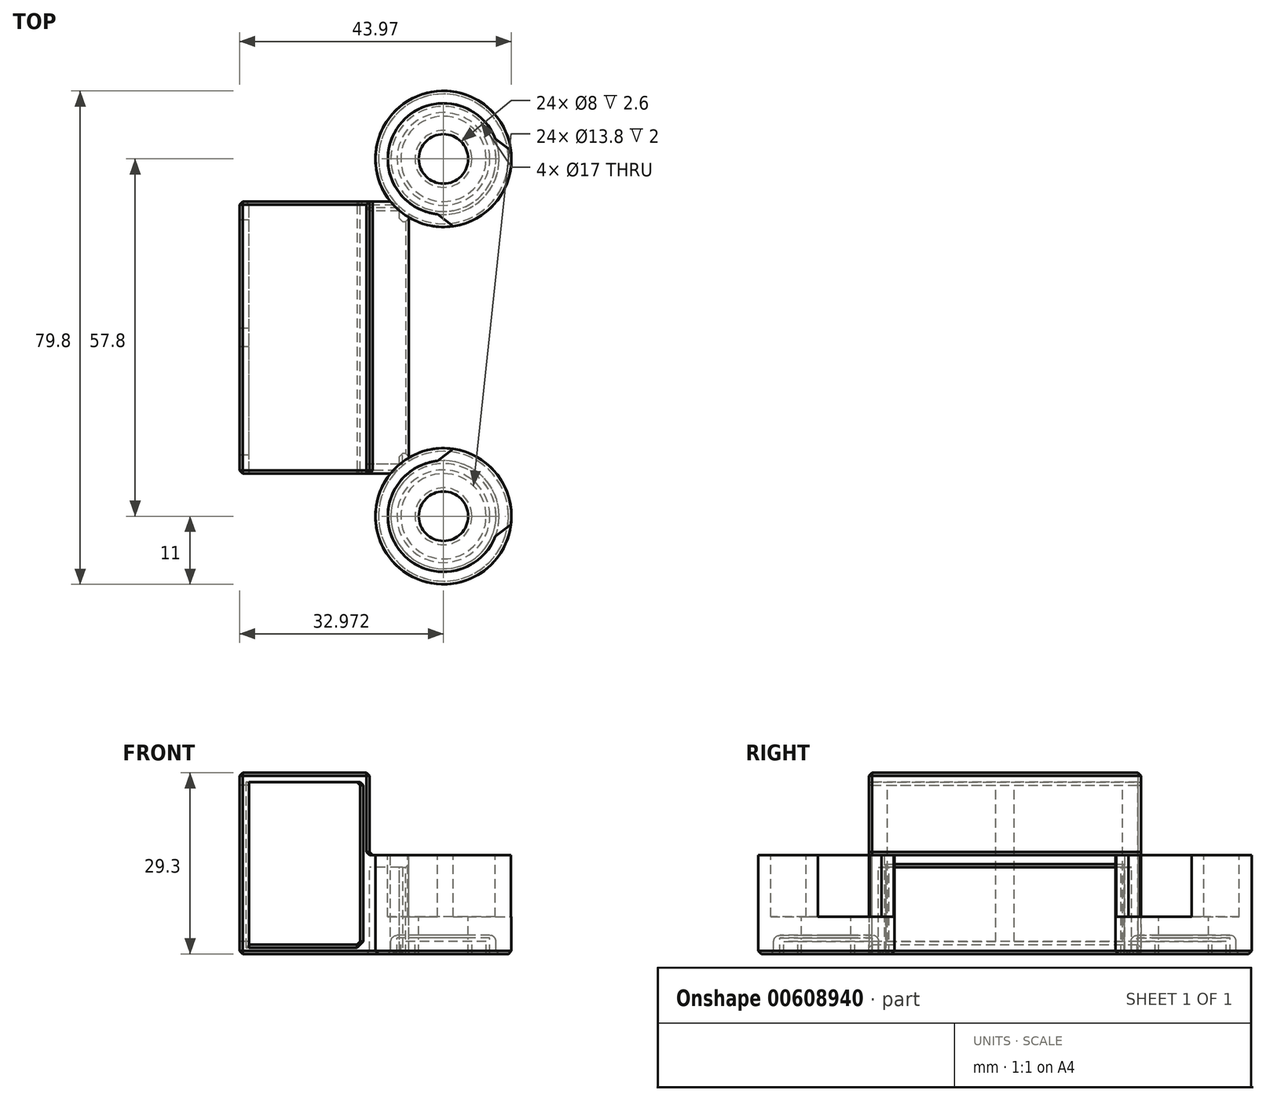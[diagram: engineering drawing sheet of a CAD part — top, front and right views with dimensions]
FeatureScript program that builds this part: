
annotation { "Feature Type Name" : "Feature", "Feature Type Description" : "" }
export const myFeature = defineFeature(function(context is Context, id is Id, definition is map)
    precondition{}
    {
        {
            var Q0;
            Q0=qCreatedBy(makeId("Front.planeOp"),FACE);
            var sketch = newSketch(context, id + "F0", { "sketchPlane" : qUnion([Q0])});
            skLineSegment(sketch, "E0.bottom", {"start": v(-19.5, 14.65) * mm, "end": v(1.5, 14.65) * mm});
            skLineSegment(sketch, "E0.top", {"start": v(-19.5, -14.65) * mm, "end": v(1.5, -14.65) * mm});
            skLineSegment(sketch, "E0.left", {"start": v(-19.5, 14.65) * mm, "end": v(-19.5, -14.65) * mm});
            skLineSegment(sketch, "E0.right", {"start": v(1.5, 14.65) * mm, "end": v(1.5, -14.65) * mm});
            skLineSegment(sketch, "E1.bottom", {"start": v(-18, 13.15) * mm, "end": v(0, 13.15) * mm});
            skLineSegment(sketch, "E1.top", {"start": v(-18, -13.15) * mm, "end": v(0, -13.15) * mm});
            skLineSegment(sketch, "E1.left", {"start": v(-18, 13.15) * mm, "end": v(-18, -13.15) * mm});
            skLineSegment(sketch, "E1.right", {"start": v(0, 13.15) * mm, "end": v(0, -13.15) * mm});
            skSolve(sketch);
        }
        {
            var Q0;
            Q0=makeQuery(id+"F0.imprint","IMPRINT",FACE,{"disambiguationData":[TD([[makeQuery(id+"F0.imprint","IMPRINT",EDGE,{"derivedFrom":sQuery(id+"F0.wireOp",EDGE,"E0.bottom")}),-1.0]])]});
            extrude(context, id + "F1", {"entities" : qUnion([Q0]), "depth" : 44 * mm, "offsetDistance" : 25 * mm});
        }
        {
            var Q0;
            Q0=makeQuery(id+"F1.opExtrude","SWEPT_FACE",FACE,{"disambiguationData":[OSD([sQuery(id+"F0.wireOp",EDGE,"E0.top")])]});
            cPlane(context, id + "F2", {"entities" : qUnion([Q0]), "cplaneType" : CPlaneType.OFFSET, "offset" : 16 * mm, "oppositeDirection" : true, "width" : 150 * mm, "height" : 150 * mm});
        }
        {
            var Q0;
            Q0=qCreatedBy(id+"F2.planeOp",FACE);
            var sketch = newSketch(context, id + "F3", { "sketchPlane" : qUnion([Q0])});
            skPoint(sketch, "E2.middle.positionSnap0", {"position": v(1.5, 22) * mm});
            skPoint(sketch, "E2.centerSnap0", {"position": v(1.5, 22) * mm});
            skLineSegment(sketch, "E3.bottom", {"start": v(1.5, 0) * mm, "end": v(7.87, 0) * mm});
            skLineSegment(sketch, "E3.top", {"start": v(1.5, 44) * mm, "end": v(7.87, 44) * mm});
            skLineSegment(sketch, "E3.left", {"start": v(1.5, 0) * mm, "end": v(1.5, 44) * mm});
            skLineSegment(sketch, "E3.right", {"start": v(7.87, 0) * mm, "end": v(7.87, 44) * mm});
            skPoint(sketch, "E3.middle", {"position": v(4.69, 22) * mm});
            skLineSegment(sketch, "E4.0", {"start": v(1.5, 42.5) * mm, "end": v(6.37, 42.5) * mm});
            skLineSegment(sketch, "E4.1", {"start": v(6.37, 1.5) * mm, "end": v(6.37, 42.5) * mm});
            skLineSegment(sketch, "E4.2", {"start": v(1.5, 1.5) * mm, "end": v(6.37, 1.5) * mm});
            skLineSegment(sketch, "E5", {"start": v(1.5, 1.5) * mm, "end": v(1.5, 42.5) * mm});
            skLineSegment(sketch, "E6", {"start": v(7.87, 3.25) * mm, "end": v(6.37, 3.25) * mm});
            skLineSegment(sketch, "E7", {"start": v(6.37, 40.75) * mm, "end": v(7.87, 40.75) * mm});
            skSolve(sketch);
        }
        {
            var Q0;
            {var subQ4=sQuery(id+"F3.wireOp",EDGE,"E3.bottom");Q0=makeQuery(id+"F3.imprint","IMPRINT",FACE,{"disambiguationData":[TD([[makeQuery(id+"F3.imprint","IMPRINT",EDGE,{"derivedFrom":subQ4}),1.0]])]});}
            var Q1;
            {var subQ0=sQuery(id+"F3.wireOp",EDGE,"E6");Q1=makeQuery(id+"F3.imprint","IMPRINT",FACE,{"disambiguationData":[TD([[makeQuery(id+"F3.imprint","IMPRINT",EDGE,{"derivedFrom":subQ0}),-1.0]])]});}
            var Q2;
            {var subQ1=sQuery(id+"F3.wireOp",EDGE,"E4.0");Q2=makeQuery(id+"F3.imprint","IMPRINT",FACE,{"disambiguationData":[TD([[makeQuery(id+"F3.imprint","IMPRINT",EDGE,{"derivedFrom":subQ1}),-1.0]])]});}
            var Q3;
            {var subQ2=sQuery(id+"F3.wireOp",EDGE,"E3.top");Q3=makeQuery(id+"F3.imprint","IMPRINT",FACE,{"disambiguationData":[TD([[makeQuery(id+"F3.imprint","IMPRINT",EDGE,{"derivedFrom":subQ2}),-1.0]])]});}
            extrude(context, id + "F4", {"entities" : qUnion([Q0, Q1, Q2, Q3]), "operationType" : NewBodyOperationType.ADD, "depth" : 2 * mm, "offsetDistance" : 25 * mm});
        }
        {
            var Q0;
            {var subQ4=sQuery(id+"F3.wireOp",EDGE,"E3.bottom");Q0=makeQuery(id+"F3.imprint","IMPRINT",FACE,{"disambiguationData":[TD([[makeQuery(id+"F3.imprint","IMPRINT",EDGE,{"derivedFrom":subQ4}),1.0]])]});}
            var Q1;
            {var subQ2=sQuery(id+"F3.wireOp",EDGE,"E3.top");Q1=makeQuery(id+"F3.imprint","IMPRINT",FACE,{"disambiguationData":[TD([[makeQuery(id+"F3.imprint","IMPRINT",EDGE,{"derivedFrom":subQ2}),-1.0]])]});}
            var Q2;
            Q2=makeQuery(id+"F1.opExtrude","SWEPT_FACE",FACE,{"disambiguationData":[OSD([sQuery(id+"F0.wireOp",EDGE,"E0.top")])]});
            extrude(context, id + "F5", {"entities" : qUnion([Q0, Q1]), "operationType" : NewBodyOperationType.ADD, "endBound" : BoundingType.UP_TO_SURFACE, "depth" : 20 * mm, "endBoundEntityFace" : qUnion([Q2]), "offsetDistance" : 25 * mm});
        }
        {
            var Q0;
            {var subQ0=sQuery(id+"F3.wireOp",EDGE,"E4.1");var subQ1=sQuery(id+"F3.wireOp",EDGE,"E3.right");var subQ2=sQuery(id+"F3.wireOp",EDGE,"E3.left");Q0=makeQuery(id+"F5.boolean.opBoolean","MERGE",FACE,{"derivedFrom":[makeQuery(id+"F1.opExtrude","SWEPT_FACE",FACE,{"disambiguationData":[OSD([sQuery(id+"F0.wireOp",EDGE,"E0.top")])]}),makeQuery(id+"F5.opExtrude","CAP_FACE",FACE,{"disambiguationData":[OSD([sQuery(id+"F3.wireOp",EDGE,"E3.bottom"),subQ2,subQ1,subQ0,sQuery(id+"F3.wireOp",EDGE,"E4.2"),sQuery(id+"F3.wireOp",EDGE,"E6")])],"isStart":false}),makeQuery(id+"F5.opExtrude","CAP_FACE",FACE,{"disambiguationData":[OSD([sQuery(id+"F3.wireOp",EDGE,"E3.top"),subQ2,subQ1,sQuery(id+"F3.wireOp",EDGE,"E4.0"),subQ0,sQuery(id+"F3.wireOp",EDGE,"E7")])],"isStart":false})]});}
            var sketch = newSketch(context, id + "F6", { "sketchPlane" : qUnion([Q0])});
            skLineSegment(sketch, "E8", {"start": v(-24.95, 22) * mm, "end": v(15.2, 22) * mm, "construction": true});
            skPoint(sketch, "E8.startSnap0", {"position": v(-19.5, 22) * mm});
            skLineSegment(sketch, "E9.0", {"start": v(-18, 0) * mm, "end": v(0, 0) * mm});
            skLineSegment(sketch, "E10.0", {"start": v(-18, 0) * mm, "end": v(0, 0) * mm, "construction": true});
            skLineSegment(sketch, "E11", {"start": v(-9, -14.84) * mm, "end": v(-9, 47.2) * mm, "construction": true});
            skPoint(sketch, "E11.startSnap0", {"position": v(-9, 0) * mm});
            skLineSegment(sketch, "E12", {"start": v(-9, 22) * mm, "end": v(20.33, -16.25) * mm, "construction": true});
            skLineSegment(sketch, "E13", {"start": v(-9, -8) * mm, "end": v(23.93, -8) * mm, "construction": true});
            skPoint(sketch, "E14", {"position": v(14, -8) * mm});
            skSolve(sketch);
        }
        {
            var Q0;
            {var subQ0=sQuery(id+"F3.wireOp",EDGE,"E3.right");Q0=makeQuery(id+"F5.boolean.opBoolean","MERGE",FACE,{"derivedFrom":[makeQuery(id+"F4.opExtrude","SWEPT_FACE",FACE,{"disambiguationData":[OSD([subQ0])]}),makeQuery(id+"F5.opExtrude","SWEPT_FACE",FACE,{"disambiguationData":[OSD([subQ0]),TDD([makeQuery(id+"F3.imprint","IMPRINT",EDGE,{"disambiguationData":[TD([[makeQuery(id+"F3.imprint","INTERSECT",VERTEX,{"derivedFrom":[sQuery(id+"F3.wireOp",EDGE,"E3.bottom"),subQ0]}),-1.0]])],"derivedFrom":subQ0})])]}),makeQuery(id+"F5.opExtrude","SWEPT_FACE",FACE,{"disambiguationData":[OSD([subQ0]),TDD([makeQuery(id+"F3.imprint","IMPRINT",EDGE,{"disambiguationData":[TD([[makeQuery(id+"F3.imprint","INTERSECT",VERTEX,{"derivedFrom":[sQuery(id+"F3.wireOp",EDGE,"E3.top"),subQ0]}),1.0]])],"derivedFrom":subQ0})])]})]});}
            cPlane(context, id + "F7", {"entities" : qUnion([Q0]), "cplaneType" : CPlaneType.OFFSET, "offset" : 5.6 * mm, "width" : 150 * mm, "height" : 150 * mm});
        }
        {
            var Q0;
            Q0=qCreatedBy(id+"F7.planeOp",FACE);
            var sketch = newSketch(context, id + "F8", { "sketchPlane" : qUnion([Q0])});
            skLineSegment(sketch, "E15", {"start": v(6.9, -11.65) * mm, "end": v(15.4, -11.65) * mm});
            skLineSegment(sketch, "E16", {"start": v(15.4, -11.65) * mm, "end": v(15.4, -14.65) * mm});
            skLineSegment(sketch, "E17", {"start": v(15.4, -14.65) * mm, "end": v(17.9, -14.65) * mm});
            skLineSegment(sketch, "E18", {"start": v(17.9, -14.65) * mm, "end": v(17.9, 1.35) * mm});
            skLineSegment(sketch, "E19", {"start": v(17.9, 1.35) * mm, "end": v(15.9, 1.35) * mm});
            skLineSegment(sketch, "E20", {"start": v(15.9, 1.35) * mm, "end": v(15.9, -8.65) * mm});
            skLineSegment(sketch, "E21", {"start": v(15.9, -8.65) * mm, "end": v(6.9, -8.65) * mm});
            skLineSegment(sketch, "E22", {"start": v(6.9, -8.65) * mm, "end": v(6.9, -11.65) * mm, "construction": true});
            skLineSegment(sketch, "E23", {"start": v(10.9, -8.65) * mm, "end": v(10.9, -11.65) * mm});
            skLineSegment(sketch, "E24", {"start": v(10.9, -14.65) * mm, "end": v(10.9, -12.05) * mm});
            skLineSegment(sketch, "E25", {"start": v(10.9, -14.65) * mm, "end": v(11.5, -14.65) * mm});
            skLineSegment(sketch, "E26", {"start": v(11.5, -14.65) * mm, "end": v(11.5, -12.65) * mm});
            skLineSegment(sketch, "E27", {"start": v(11.5, -12.05) * mm, "end": v(10.9, -12.05) * mm});
            skPoint(sketch, "E28.visualSharp", {"position": v(17.9, -14.65) * mm});
            skLineSegment(sketch, "E29", {"start": v(17.9, -14.15) * mm, "end": v(17.4, -14.65) * mm});
            skLineSegment(sketch, "E30", {"start": v(15.4, -14.15) * mm, "end": v(15.9, -14.65) * mm});
            skLineSegment(sketch, "E31", {"start": v(11.5, -12.05) * mm, "end": v(14.4, -12.05) * mm});
            skLineSegment(sketch, "E32", {"start": v(14.4, -12.05) * mm, "end": v(14.4, -14.65) * mm});
            skLineSegment(sketch, "E33", {"start": v(14.4, -14.65) * mm, "end": v(13.8, -14.65) * mm});
            skLineSegment(sketch, "E34", {"start": v(13.8, -14.65) * mm, "end": v(13.8, -12.65) * mm});
            skLineSegment(sketch, "E35", {"start": v(13.8, -12.65) * mm, "end": v(11.5, -12.65) * mm});
            skSolve(sketch);
        }
        {
            var Q0;
            Q0=makeQuery(id+"F8.imprint","IMPRINT",FACE,{"disambiguationData":[TD([[makeQuery(id+"F8.imprint","IMPRINT",EDGE,{"derivedFrom":sQuery(id+"F8.wireOp",EDGE,"E15")}),1.0]])]});
            var Q1;
            Q1=makeQuery(id+"F8.imprint","IMPRINT",FACE,{"disambiguationData":[TD([[makeQuery(id+"F8.imprint","IMPRINT",EDGE,{"derivedFrom":sQuery(id+"F8.wireOp",EDGE,"E24")}),-1.0]])]});
            var Q2;
            Q2=sQuery(id+"F8.wireOp",EDGE,"E22");
            revolve(context, id + "F9", {"entities" : qUnion([Q0, Q1]), "axis" : qUnion([Q2]), "revolveType" : RevolveType.FULL});
        }
        {
            var Q0;
            Q0=makeQuery(id+"F9.opRevolve","SWEPT_EDGE",EDGE,{"disambiguationData":[OSD([sQuery(id+"F8.wireOp",EDGE,"E15"),sQuery(id+"F8.wireOp",EDGE,"E16")])]});
            fillet(context, id + "F10", {"entities" : qUnion([Q0]), "radius" : 1 * mm, "tangentPropagation" : true, "allowEdgeOverflow" : false});
        }
        {
            var Q0;
            Q0=makeQuery(id+"F9.opRevolve","SWEPT_FACE",FACE,{"disambiguationData":[OSD([sQuery(id+"F8.wireOp",EDGE,"E19")])]});
            var sketch = newSketch(context, id + "F11", { "sketchPlane" : qUnion([Q0])});
            skLineSegment(sketch, "E36.0", {"start": v(-9, -22) * mm, "end": v(20.33, 16.25) * mm});
            skPoint(sketch, "E37.0", {"position": v(13.47, 6.9) * mm});
            skLineSegment(sketch, "E38.0", {"start": v(-9, -22) * mm, "end": v(20.33, 16.25) * mm, "construction": true});
            skLineSegment(sketch, "E39.right", {"start": v(8.79, 0.79) * mm, "end": v(18.16, 13.01) * mm});
            skLineSegment(sketch, "E40", {"start": v(18.16, 13.01) * mm, "end": v(26.99, 6.24) * mm});
            skLineSegment(sketch, "E41", {"start": v(26.99, 6.24) * mm, "end": v(17.61, -5.98) * mm});
            skLineSegment(sketch, "E42", {"start": v(17.61, -5.98) * mm, "end": v(8.79, 0.79) * mm});
            skLineSegment(sketch, "E43", {"start": v(22.3, 0.13) * mm, "end": v(13.47, 6.9) * mm, "construction": true});
            skLineSegment(sketch, "E44", {"start": v(13.47, 6.9) * mm, "end": v(4.35, 13.9) * mm, "construction": true});
            skSolve(sketch);
        }
        {
            var Q0;
            {var subQ0=sQuery(id+"F11.wireOp",EDGE,"E40");var subQ1=sQuery(id+"F8.wireOp",EDGE,"E19");var subQ2=makeQuery(id+"F9.opRevolve","SWEPT_EDGE",EDGE,{"disambiguationData":[OSD([sQuery(id+"F8.wireOp",EDGE,"E18"),subQ1])]});var subQ3=makeQuery(id+"F11.imprint","INTERSECT",VERTEX,{"derivedFrom":[subQ2,subQ0]});Q0=makeQuery(id+"F11.imprint","IMPRINT",FACE,{"disambiguationData":[TD([[makeQuery(id+"F11.imprint","IMPRINT",EDGE,{"disambiguationData":[TD([[subQ3,1.0]])],"derivedFrom":subQ0}),-1.0]])]});}
            extrude(context, id + "F12", {"entities" : qUnion([Q0]), "operationType" : NewBodyOperationType.REMOVE, "oppositeDirection" : true, "depth" : 10 * mm, "offsetDistance" : 25 * mm});
        }
        {
            var Q0;
            Q0=sQuery(id+"F6.wireOp",EDGE,"E8");
            cPlane(context, id + "F13", {"entities" : qUnion([Q0]), "cplaneType" : CPlaneType.LINE_ANGLE, "offset" : 12.5 * mm, "angle" : 0 * degree, "width" : 150 * mm, "height" : 150 * mm});
        }
        {
            var Q0;
            Q0=makeQuery(id+"F9.opRevolve","SWEPT_BODY",BODY,{"disambiguationData":[OSD([sQuery(id+"F8.wireOp",EDGE,"E15"),sQuery(id+"F8.wireOp",EDGE,"E16"),sQuery(id+"F8.wireOp",EDGE,"E17"),sQuery(id+"F8.wireOp",EDGE,"E18"),sQuery(id+"F8.wireOp",EDGE,"E19"),sQuery(id+"F8.wireOp",EDGE,"E20"),sQuery(id+"F8.wireOp",EDGE,"E21"),sQuery(id+"F8.wireOp",EDGE,"E23"),sQuery(id+"F8.wireOp",EDGE,"E29"),sQuery(id+"F8.wireOp",EDGE,"E30")])]});
            var Q1;
            Q1=makeQuery(id+"F9.opRevolve","SWEPT_BODY",BODY,{"disambiguationData":[OSD([sQuery(id+"F8.wireOp",EDGE,"E24"),sQuery(id+"F8.wireOp",EDGE,"E25"),sQuery(id+"F8.wireOp",EDGE,"E26"),sQuery(id+"F8.wireOp",EDGE,"E27")])]});
            var Q2;
            Q2=qCreatedBy(id+"F13.planeOp",FACE);
            mirror(context, id + "F14", {"entities" : qUnion([Q0, Q1]), "mirrorPlane" : qUnion([Q2])});
        }
        {
            var Q0;
            Q0=makeQuery(id+"F14.opPattern","COPY",BODY,{"derivedFrom":makeQuery(id+"F9.opRevolve","SWEPT_BODY",BODY,{"disambiguationData":[OSD([sQuery(id+"F8.wireOp",EDGE,"E15"),sQuery(id+"F8.wireOp",EDGE,"E16"),sQuery(id+"F8.wireOp",EDGE,"E17"),sQuery(id+"F8.wireOp",EDGE,"E18"),sQuery(id+"F8.wireOp",EDGE,"E19"),sQuery(id+"F8.wireOp",EDGE,"E20"),sQuery(id+"F8.wireOp",EDGE,"E21"),sQuery(id+"F8.wireOp",EDGE,"E23"),sQuery(id+"F8.wireOp",EDGE,"E29"),sQuery(id+"F8.wireOp",EDGE,"E30")])]}),"instanceName":"1"});
            var Q1;
            Q1=makeQuery(id+"F9.opRevolve","SWEPT_BODY",BODY,{"disambiguationData":[OSD([sQuery(id+"F8.wireOp",EDGE,"E15"),sQuery(id+"F8.wireOp",EDGE,"E16"),sQuery(id+"F8.wireOp",EDGE,"E17"),sQuery(id+"F8.wireOp",EDGE,"E18"),sQuery(id+"F8.wireOp",EDGE,"E19"),sQuery(id+"F8.wireOp",EDGE,"E20"),sQuery(id+"F8.wireOp",EDGE,"E21"),sQuery(id+"F8.wireOp",EDGE,"E23"),sQuery(id+"F8.wireOp",EDGE,"E29"),sQuery(id+"F8.wireOp",EDGE,"E30")])]});
            var Q2;
            Q2=makeQuery(id+"F1.opExtrude","SWEPT_BODY",BODY,{"disambiguationData":[OSD([sQuery(id+"F0.wireOp",EDGE,"E0.bottom"),sQuery(id+"F0.wireOp",EDGE,"E0.top"),sQuery(id+"F0.wireOp",EDGE,"E0.left"),sQuery(id+"F0.wireOp",EDGE,"E0.right"),sQuery(id+"F0.wireOp",EDGE,"E1.bottom"),sQuery(id+"F0.wireOp",EDGE,"E1.top"),sQuery(id+"F0.wireOp",EDGE,"E1.left"),sQuery(id+"F0.wireOp",EDGE,"E1.right")])]});
            booleanBodies(context, id + "F15", {"operationType" : BooleanOperationType.UNION, "tools" : qUnion([Q0, Q1, Q2])});
        }
        {
            var Q0;
            Q0=makeQuery(id+"F1.opExtrude","SWEPT_FACE",FACE,{"disambiguationData":[OSD([sQuery(id+"F0.wireOp",EDGE,"E0.left")])]});
            var sketch = newSketch(context, id + "F16", { "sketchPlane" : qUnion([Q0])});
            skLineSegment(sketch, "E45.bottom", {"start": v(41, -12.65) * mm, "end": v(23.5, -12.65) * mm});
            skLineSegment(sketch, "E45.top", {"start": v(41, 12.65) * mm, "end": v(23.5, 12.65) * mm});
            skLineSegment(sketch, "E45.left", {"start": v(41, -12.65) * mm, "end": v(41, 12.65) * mm});
            skLineSegment(sketch, "E45.right", {"start": v(23.5, -12.65) * mm, "end": v(23.5, 12.65) * mm});
            skLineSegment(sketch, "E46.bottom", {"start": v(20.5, -12.65) * mm, "end": v(3, -12.65) * mm});
            skLineSegment(sketch, "E46.top", {"start": v(20.5, 12.65) * mm, "end": v(3, 12.65) * mm});
            skLineSegment(sketch, "E46.left", {"start": v(20.5, -12.65) * mm, "end": v(20.5, 12.65) * mm});
            skLineSegment(sketch, "E46.right", {"start": v(3, -12.65) * mm, "end": v(3, 12.65) * mm});
            skSolve(sketch);
        }
        {
            var Q0;
            Q0=makeQuery(id+"F16.imprint","IMPRINT",FACE,{"disambiguationData":[TD([[makeQuery(id+"F16.imprint","IMPRINT",EDGE,{"derivedFrom":sQuery(id+"F16.wireOp",EDGE,"E46.bottom")}),-1.0]])]});
            var Q1;
            Q1=makeQuery(id+"F16.imprint","IMPRINT",FACE,{"disambiguationData":[TD([[makeQuery(id+"F16.imprint","IMPRINT",EDGE,{"derivedFrom":sQuery(id+"F16.wireOp",EDGE,"E45.bottom")}),-1.0]])]});
            var Q2;
            Q2=makeQuery(id+"F1.opExtrude","SWEPT_FACE",FACE,{"disambiguationData":[OSD([sQuery(id+"F0.wireOp",EDGE,"E1.left")])]});
            extrude(context, id + "F17", {"entities" : qUnion([Q0, Q1]), "operationType" : NewBodyOperationType.REMOVE, "endBound" : BoundingType.UP_TO_SURFACE, "oppositeDirection" : true, "depth" : 25 * mm, "endBoundEntityFace" : qUnion([Q2]), "offsetDistance" : 25 * mm});
        }
        {
            var Q0;
            Q0=makeQuery(id+"F1.opExtrude","SWEPT_EDGE",EDGE,{"disambiguationData":[OSD([sQuery(id+"F0.wireOp",EDGE,"E0.bottom"),sQuery(id+"F0.wireOp",EDGE,"E0.left")])]});
            var Q1;
            Q1=makeQuery(id+"F1.opExtrude","SWEPT_EDGE",EDGE,{"disambiguationData":[OSD([sQuery(id+"F0.wireOp",EDGE,"E0.top"),sQuery(id+"F0.wireOp",EDGE,"E0.left")])]});
            var Q2;
            Q2=makeQuery(id+"F1.opExtrude","CAP_EDGE",EDGE,{"disambiguationData":[OSD([sQuery(id+"F0.wireOp",EDGE,"E0.left")])],"isStart":true});
            var Q3;
            Q3=makeQuery(id+"F1.opExtrude","CAP_EDGE",EDGE,{"disambiguationData":[OSD([sQuery(id+"F0.wireOp",EDGE,"E0.left")])],"isStart":false});
            var Q4;
            Q4=makeQuery(id+"F1.opExtrude","SWEPT_EDGE",EDGE,{"disambiguationData":[OSD([sQuery(id+"F0.wireOp",EDGE,"E0.bottom"),sQuery(id+"F0.wireOp",EDGE,"E0.right")])]});
            var Q5;
            Q5=makeQuery(id+"F1.opExtrude","CAP_EDGE",EDGE,{"disambiguationData":[OSD([sQuery(id+"F0.wireOp",EDGE,"E0.bottom")])],"isStart":true});
            var Q6;
            Q6=makeQuery(id+"F1.opExtrude","CAP_EDGE",EDGE,{"disambiguationData":[OSD([sQuery(id+"F0.wireOp",EDGE,"E0.bottom")])],"isStart":false});
            var Q7;
            Q7=makeQuery(id+"F17.boolean.opBoolean","COPY",EDGE,{"derivedFrom":makeQuery(id+"F17.opExtrude","CAP_EDGE",EDGE,{"disambiguationData":[OSD([sQuery(id+"F16.wireOp",EDGE,"E45.right")])],"isStart":true})});
            var Q8;
            Q8=makeQuery(id+"F17.boolean.opBoolean","COPY",EDGE,{"derivedFrom":makeQuery(id+"F17.opExtrude","CAP_EDGE",EDGE,{"disambiguationData":[OSD([sQuery(id+"F16.wireOp",EDGE,"E45.top")])],"isStart":true})});
            var Q9;
            Q9=makeQuery(id+"F17.boolean.opBoolean","COPY",EDGE,{"derivedFrom":makeQuery(id+"F17.opExtrude","CAP_EDGE",EDGE,{"disambiguationData":[OSD([sQuery(id+"F16.wireOp",EDGE,"E45.top")])],"isStart":false})});
            var Q10;
            Q10=makeQuery(id+"F17.boolean.opBoolean","COPY",EDGE,{"derivedFrom":makeQuery(id+"F17.opExtrude","CAP_EDGE",EDGE,{"disambiguationData":[OSD([sQuery(id+"F16.wireOp",EDGE,"E45.right")])],"isStart":false})});
            var Q11;
            Q11=makeQuery(id+"F17.boolean.opBoolean","COPY",EDGE,{"derivedFrom":makeQuery(id+"F17.opExtrude","CAP_EDGE",EDGE,{"disambiguationData":[OSD([sQuery(id+"F16.wireOp",EDGE,"E46.left")])],"isStart":false})});
            var Q12;
            Q12=makeQuery(id+"F17.boolean.opBoolean","COPY",EDGE,{"derivedFrom":makeQuery(id+"F17.opExtrude","CAP_EDGE",EDGE,{"disambiguationData":[OSD([sQuery(id+"F16.wireOp",EDGE,"E46.right")])],"isStart":false})});
            var Q13;
            Q13=makeQuery(id+"F1.opExtrude","CAP_EDGE",EDGE,{"disambiguationData":[OSD([sQuery(id+"F0.wireOp",EDGE,"E1.left")])],"isStart":true});
            var Q14;
            Q14=makeQuery(id+"F17.boolean.opBoolean","COPY",EDGE,{"derivedFrom":makeQuery(id+"F17.opExtrude","CAP_EDGE",EDGE,{"disambiguationData":[OSD([sQuery(id+"F16.wireOp",EDGE,"E45.bottom")])],"isStart":false})});
            var Q15;
            Q15=makeQuery(id+"F17.boolean.opBoolean","COPY",EDGE,{"derivedFrom":makeQuery(id+"F17.opExtrude","CAP_EDGE",EDGE,{"disambiguationData":[OSD([sQuery(id+"F16.wireOp",EDGE,"E46.bottom")])],"isStart":false})});
            var Q16;
            Q16=makeQuery(id+"F17.boolean.opBoolean","COPY",EDGE,{"derivedFrom":makeQuery(id+"F17.opExtrude","CAP_EDGE",EDGE,{"disambiguationData":[OSD([sQuery(id+"F16.wireOp",EDGE,"E45.left")])],"isStart":false})});
            var Q17;
            Q17=makeQuery(id+"F1.opExtrude","CAP_EDGE",EDGE,{"disambiguationData":[OSD([sQuery(id+"F0.wireOp",EDGE,"E1.top")])],"isStart":false});
            var Q18;
            Q18=makeQuery(id+"F1.opExtrude","CAP_EDGE",EDGE,{"disambiguationData":[OSD([sQuery(id+"F0.wireOp",EDGE,"E1.top")])],"isStart":true});
            var Q19;
            Q19=makeQuery(id+"F1.opExtrude","CAP_EDGE",EDGE,{"disambiguationData":[OSD([sQuery(id+"F0.wireOp",EDGE,"E1.right")])],"isStart":true});
            var Q20;
            Q20=makeQuery(id+"F1.opExtrude","CAP_EDGE",EDGE,{"disambiguationData":[OSD([sQuery(id+"F0.wireOp",EDGE,"E1.right")])],"isStart":false});
            var Q21;
            Q21=makeQuery(id+"F1.opExtrude","SWEPT_EDGE",EDGE,{"disambiguationData":[OSD([sQuery(id+"F0.wireOp",EDGE,"E1.top"),sQuery(id+"F0.wireOp",EDGE,"E1.right")])]});
            var Q22;
            Q22=makeQuery(id+"F1.opExtrude","SWEPT_EDGE",EDGE,{"disambiguationData":[OSD([sQuery(id+"F0.wireOp",EDGE,"E1.bottom"),sQuery(id+"F0.wireOp",EDGE,"E1.right")])]});
            var Q23;
            Q23=makeQuery(id+"F4.opExtrude","CAP_EDGE",EDGE,{"disambiguationData":[OSD([sQuery(id+"F3.wireOp",EDGE,"E3.left"),sQuery(id+"F3.wireOp",EDGE,"E5")])],"isStart":true});
            var Q24;
            {var subQ0=sQuery(id+"F0.wireOp",EDGE,"E0.right");var subQ1=sQuery(id+"F0.wireOp",EDGE,"E0.bottom");Q24=makeQuery(id+"F4.boolean.opBoolean","SPLIT",EDGE,{"disambiguationData":[TD([makeQuery(id+"F1.opExtrude","SWEPT_FACE",FACE,{"disambiguationData":[OSD([subQ1])]})])],"derivedFrom":makeQuery(id+"F1.opExtrude","CAP_EDGE",EDGE,{"disambiguationData":[OSD([subQ0])],"isStart":false})});}
            var Q25;
            Q25=makeQuery(id+"F5.opExtrude","SWEPT_EDGE",EDGE,{"disambiguationData":[OSD([sQuery(id+"F3.wireOp",EDGE,"E3.right"),sQuery(id+"F3.wireOp",EDGE,"E6")])]});
            var Q26;
            Q26=makeQuery(id+"F4.opExtrude","CAP_EDGE",EDGE,{"disambiguationData":[OSD([sQuery(id+"F3.wireOp",EDGE,"E3.right")])],"isStart":false});
            var Q27;
            Q27=makeQuery(id+"F5.opExtrude","SWEPT_EDGE",EDGE,{"disambiguationData":[OSD([sQuery(id+"F3.wireOp",EDGE,"E3.right"),sQuery(id+"F3.wireOp",EDGE,"E7")])]});
            var Q28;
            Q28=makeQuery(id+"F5.opExtrude","SWEPT_EDGE",EDGE,{"disambiguationData":[OSD([sQuery(id+"F3.wireOp",EDGE,"E4.1"),sQuery(id+"F3.wireOp",EDGE,"E7")])]});
            var Q29;
            {var subQ0=sQuery(id+"F3.wireOp",EDGE,"E4.1");Q29=makeQuery(id+"F5.opExtrude","CAP_EDGE",EDGE,{"disambiguationData":[OSD([subQ0]),TDD([makeQuery(id+"F3.imprint","IMPRINT",EDGE,{"disambiguationData":[TD([[makeQuery(id+"F3.imprint","INTERSECT",VERTEX,{"derivedFrom":[sQuery(id+"F3.wireOp",EDGE,"E4.0"),subQ0]}),1.0]])],"derivedFrom":subQ0})])],"isStart":false});}
            var Q30;
            {var subQ0=sQuery(id+"F0.wireOp",EDGE,"E0.left");var subQ4=sQuery(id+"F0.wireOp",EDGE,"E0.top");var subQ6=sQuery(id+"F3.wireOp",EDGE,"E3.top");Q30=makeQuery(id+"F15.opBoolean","SPLIT",EDGE,{"disambiguationData":[TD([makeQuery(id+"F1.opExtrude","SWEPT_FACE",FACE,{"disambiguationData":[OSD([subQ0])]})])],"derivedFrom":makeQuery(id+"F5.boolean.opBoolean","MERGE",EDGE,{"derivedFrom":[makeQuery(id+"F1.opExtrude","CAP_EDGE",EDGE,{"disambiguationData":[OSD([subQ4])],"isStart":false}),makeQuery(id+"F5.opExtrude","CAP_EDGE",EDGE,{"disambiguationData":[OSD([subQ6])],"isStart":false})]})});}
            var Q31;
            Q31=makeQuery(id+"F1.opExtrude","SWEPT_EDGE",EDGE,{"disambiguationData":[OSD([sQuery(id+"F0.wireOp",EDGE,"E0.top"),sQuery(id+"F0.wireOp",EDGE,"E0.right")])]});
            var Q32;
            Q32=makeQuery(id+"F5.opExtrude","CAP_EDGE",EDGE,{"disambiguationData":[OSD([sQuery(id+"F3.wireOp",EDGE,"E4.2")])],"isStart":false});
            var Q33;
            Q33=makeQuery(id+"F5.opExtrude","SWEPT_EDGE",EDGE,{"disambiguationData":[OSD([sQuery(id+"F3.wireOp",EDGE,"E4.1"),sQuery(id+"F3.wireOp",EDGE,"E6")])]});
            var Q34;
            Q34=makeQuery(id+"F17.boolean.opBoolean","COPY",EDGE,{"derivedFrom":makeQuery(id+"F17.opExtrude","CAP_EDGE",EDGE,{"disambiguationData":[OSD([sQuery(id+"F16.wireOp",EDGE,"E46.top")])],"isStart":true})});
            var Q35;
            Q35=makeQuery(id+"F17.boolean.opBoolean","COPY",EDGE,{"derivedFrom":makeQuery(id+"F17.opExtrude","CAP_EDGE",EDGE,{"disambiguationData":[OSD([sQuery(id+"F16.wireOp",EDGE,"E46.top")])],"isStart":false})});
            var Q36;
            Q36=makeQuery(id+"F17.boolean.opBoolean","COPY",EDGE,{"derivedFrom":makeQuery(id+"F17.opExtrude","CAP_EDGE",EDGE,{"disambiguationData":[OSD([sQuery(id+"F16.wireOp",EDGE,"E46.left")])],"isStart":true})});
            var Q37;
            Q37=makeQuery(id+"F17.boolean.opBoolean","COPY",EDGE,{"derivedFrom":makeQuery(id+"F17.opExtrude","CAP_EDGE",EDGE,{"disambiguationData":[OSD([sQuery(id+"F16.wireOp",EDGE,"E45.left")])],"isStart":true})});
            var Q38;
            Q38=makeQuery(id+"F17.boolean.opBoolean","COPY",EDGE,{"derivedFrom":makeQuery(id+"F17.opExtrude","CAP_EDGE",EDGE,{"disambiguationData":[OSD([sQuery(id+"F16.wireOp",EDGE,"E46.right")])],"isStart":true})});
            var Q39;
            Q39=makeQuery(id+"F17.boolean.opBoolean","COPY",EDGE,{"derivedFrom":makeQuery(id+"F17.opExtrude","CAP_EDGE",EDGE,{"disambiguationData":[OSD([sQuery(id+"F16.wireOp",EDGE,"E46.bottom")])],"isStart":true})});
            var Q40;
            Q40=makeQuery(id+"F17.boolean.opBoolean","COPY",EDGE,{"derivedFrom":makeQuery(id+"F17.opExtrude","CAP_EDGE",EDGE,{"disambiguationData":[OSD([sQuery(id+"F16.wireOp",EDGE,"E45.bottom")])],"isStart":true})});
            var Q41;
            {var subQ0=sQuery(id+"F3.wireOp",EDGE,"E3.bottom");var subQ1=sQuery(id+"F0.wireOp",EDGE,"E0.left");var subQ5=sQuery(id+"F0.wireOp",EDGE,"E0.top");Q41=makeQuery(id+"F15.opBoolean","SPLIT",EDGE,{"disambiguationData":[TD([makeQuery(id+"F1.opExtrude","SWEPT_FACE",FACE,{"disambiguationData":[OSD([subQ1])]})])],"derivedFrom":makeQuery(id+"F5.boolean.opBoolean","MERGE",EDGE,{"derivedFrom":[makeQuery(id+"F1.opExtrude","CAP_EDGE",EDGE,{"disambiguationData":[OSD([subQ5])],"isStart":true}),makeQuery(id+"F5.opExtrude","CAP_EDGE",EDGE,{"disambiguationData":[OSD([subQ0])],"isStart":false})]})});}
            chamfer(context, id + "F18", {"entities" : qUnion([Q0, Q1, Q2, Q3, Q4, Q5, Q6, Q7, Q8, Q9, Q10, Q11, Q12, Q13, Q14, Q15, Q16, Q17, Q18, Q19, Q20, Q21, Q22, Q23, Q24, Q25, Q26, Q27, Q28, Q29, Q30, Q31, Q32, Q33, Q34, Q35, Q36, Q37, Q38, Q39, Q40, Q41]), "width" : .5 * mm, "tangentPropagation" : true});
        }
    });
